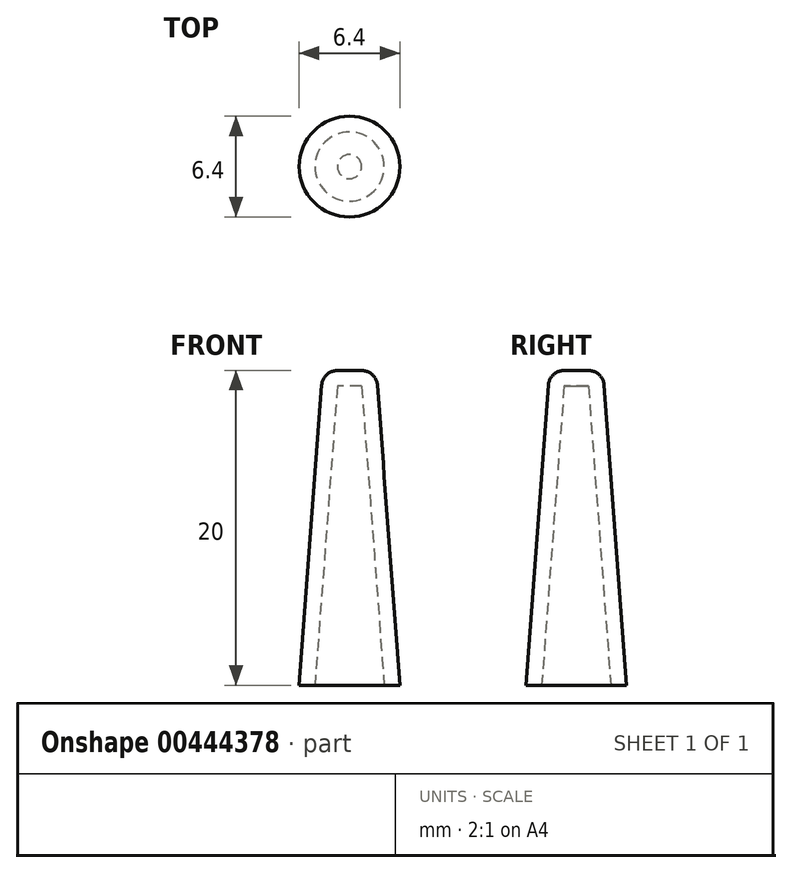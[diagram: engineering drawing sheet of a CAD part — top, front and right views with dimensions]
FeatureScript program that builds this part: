
annotation { "Feature Type Name" : "Feature", "Feature Type Description" : "" }
export const myFeature = defineFeature(function(context is Context, id is Id, definition is map)
    precondition{}
    {
        {
            var Q0;
            Q0=qCreatedBy(makeId("Top.planeOp"),FACE);
            var sketch = newSketch(context, id + "F0", { "sketchPlane" : qUnion([Q0])});
            skCircle(sketch, "E0", {"center": v(0, 0) * mm, "radius": 3.2 * mm});
            skSolve(sketch);
        }
        {
            var Q0;
            Q0=qCreatedBy(makeId("Top.planeOp"),FACE);
            cPlane(context, id + "F1", {"entities" : qUnion([Q0]), "cplaneType" : CPlaneType.OFFSET, "offset" : 20 * mm, "width" : 150 * mm, "height" : 150 * mm});
        }
        {
            var Q0;
            Q0=qCreatedBy(id+"F1.planeOp",FACE);
            var sketch = newSketch(context, id + "F2", { "sketchPlane" : qUnion([Q0])});
            skCircle(sketch, "E1", {"center": v(0, 0) * mm, "radius": 1.7 * mm});
            skSolve(sketch);
        }
        {
            var Q0;
            Q0=makeQuery(id+"F0.imprint","IMPRINT",FACE,{"disambiguationData":[TD([[makeQuery(id+"F0.imprint","IMPRINT",EDGE,{"derivedFrom":sQuery(id+"F0.wireOp",EDGE,"E0")}),1.0]])]});
            var Q1;
            Q1=makeQuery(id+"F2.imprint","IMPRINT",FACE,{"disambiguationData":[TD([[makeQuery(id+"F2.imprint","IMPRINT",EDGE,{"derivedFrom":sQuery(id+"F2.wireOp",EDGE,"E1")}),1.0]])]});
            loft(context, id + "F3", {"sheetProfilesArray" : [{ "sheetProfileEntities" : qUnion([Q0]) }, { "sheetProfileEntities" : qUnion([Q1]) }]});
        }
        {
            var Q0;
            Q0=makeQuery(id+"F3.opLoft","CAP_FACE",FACE,{"disambiguationData":[OSD([makeQuery(id+"F0.imprint","IMPRINT",FACE,{"disambiguationData":[TD([[makeQuery(id+"F0.imprint","IMPRINT",EDGE,{"derivedFrom":sQuery(id+"F0.wireOp",EDGE,"E0")}),1.0]])]})])],"isStart":true});
            shell(context, id + "F4", {"entities" : qUnion([Q0]), "thickness" : 1 * mm});
        }
        {
            var Q0;
            Q0=makeQuery(id+"F3.opLoft","MID_CAP_EDGE",EDGE,{"disambiguationData":[OSD([sQuery(id+"F0.wireOp",EDGE,"E0"),sQuery(id+"F2.wireOp",EDGE,"E1")])],"capPos":1.0});
            fillet(context, id + "F5", {"entities" : qUnion([Q0]), "radius" : 1 * mm, "tangentPropagation" : true, "allowEdgeOverflow" : false});
        }
    });
